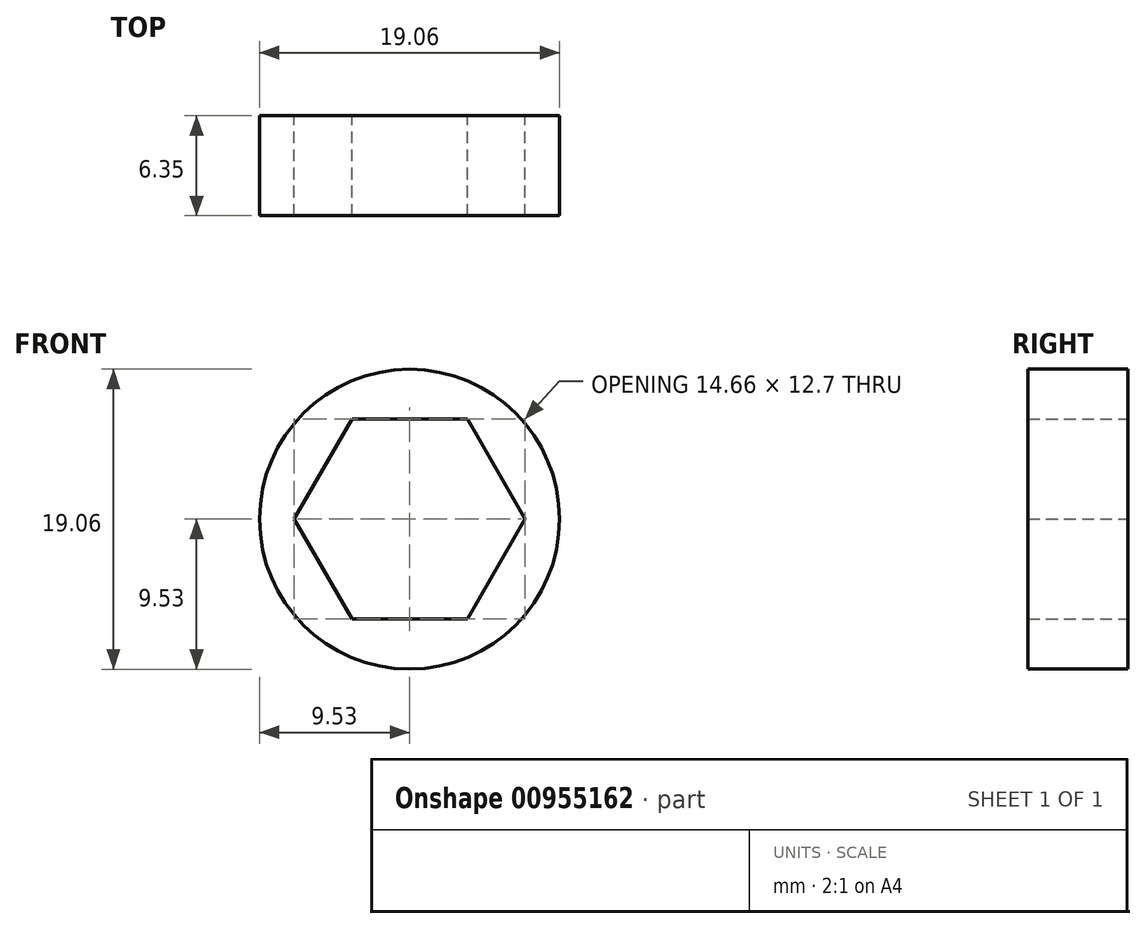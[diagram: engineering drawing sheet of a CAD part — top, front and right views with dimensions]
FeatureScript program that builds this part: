
annotation { "Feature Type Name" : "Feature", "Feature Type Description" : "" }
export const myFeature = defineFeature(function(context is Context, id is Id, definition is map)
    precondition{}
    {
        {
            var Q0;
            Q0=qCreatedBy(makeId("Front.planeOp"),FACE);
            var sketch = newSketch(context, id + "F0", { "sketchPlane" : qUnion([Q0])});
            skCircle(sketch, "E0.cCircle", {"center": v(0, 0) * mm, "radius": 6.35 * mm, "construction": true});
            skLineSegment(sketch, "E0.0", {"start": v(-3.67, 6.35) * mm, "end": v(3.67, 6.35) * mm});
            skLineSegment(sketch, "E0.1", {"start": v(3.67, 6.35) * mm, "end": v(7.33, 0) * mm});
            skLineSegment(sketch, "E0.2", {"start": v(7.33, 0) * mm, "end": v(3.67, -6.35) * mm});
            skLineSegment(sketch, "E0.3", {"start": v(3.67, -6.35) * mm, "end": v(-3.67, -6.35) * mm});
            skLineSegment(sketch, "E0.4", {"start": v(-3.67, -6.35) * mm, "end": v(-7.33, 0) * mm});
            skLineSegment(sketch, "E0.5", {"start": v(-7.33, 0) * mm, "end": v(-3.67, 6.35) * mm});
            skPoint(sketch, "E0.0.midPoint", {"position": v(0, 6.35) * mm});
            skCircle(sketch, "E1", {"center": v(0, 0) * mm, "radius": 9.53 * mm});
            skSolve(sketch);
        }
        {
            var Q0;
            Q0=qSketchRegion(id+"F0",true);
            extrude(context, id + "F1", {"entities" : qUnion([Q0]), "depth" : 6.35 * mm, "offsetDistance" : 25.4 * mm});
        }
    });
